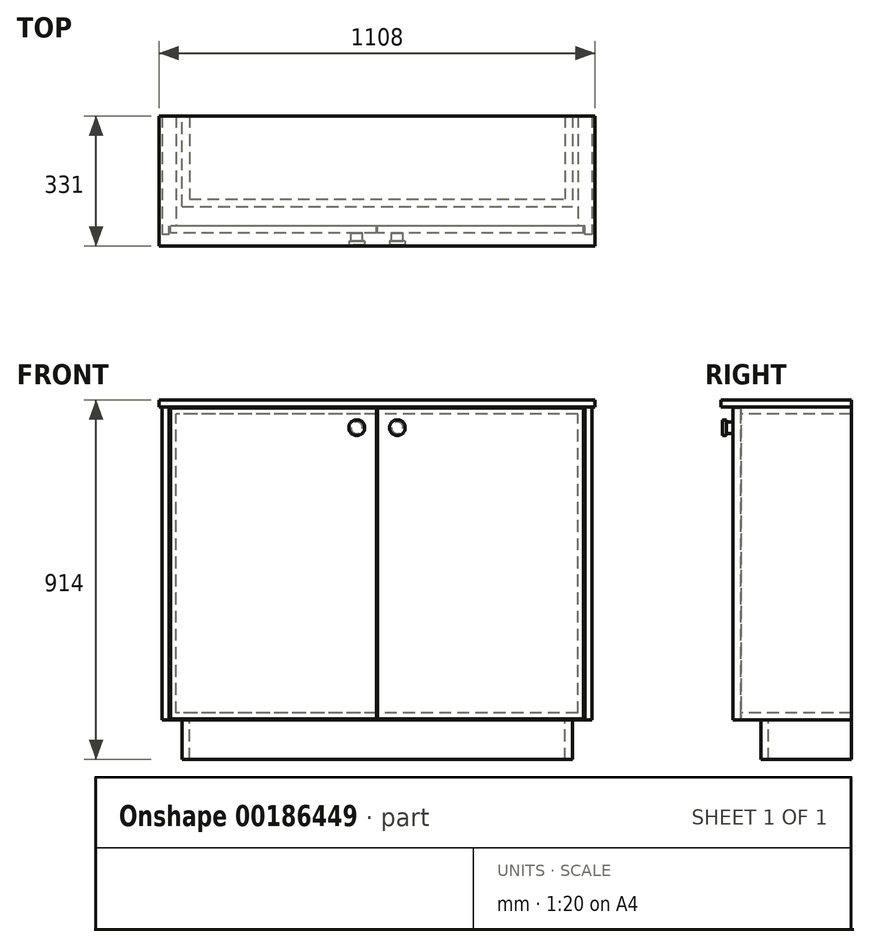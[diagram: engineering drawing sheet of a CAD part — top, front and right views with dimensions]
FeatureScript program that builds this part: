
annotation { "Feature Type Name" : "Feature", "Feature Type Description" : "" }
export const myFeature = defineFeature(function(context is Context, id is Id, definition is map)
    precondition{}
    {
        {
            var Q0;
            Q0=qCreatedBy(makeId("Front.planeOp"),FACE);
            var sketch = newSketch(context, id + "F0", { "sketchPlane" : qUnion([Q0])});
            skLineSegment(sketch, "E0.bottom", {"start": v(528, -398) * mm, "end": v(-528, -398) * mm});
            skLineSegment(sketch, "E0.top", {"start": v(528, 398) * mm, "end": v(-528, 398) * mm});
            skLineSegment(sketch, "E0.left", {"start": v(528, -398) * mm, "end": v(528, 398) * mm});
            skLineSegment(sketch, "E0.right", {"start": v(-528, -398) * mm, "end": v(-528, 398) * mm});
            skPoint(sketch, "E0.middle", {"position": v(0, 0) * mm});
            skLineSegment(sketch, "E1.0", {"start": v(510, -380) * mm, "end": v(-510, -380) * mm});
            skLineSegment(sketch, "E1.1", {"start": v(510, -380) * mm, "end": v(510, 380) * mm});
            skLineSegment(sketch, "E1.2", {"start": v(510, 380) * mm, "end": v(-510, 380) * mm});
            skLineSegment(sketch, "E1.3", {"start": v(-510, -380) * mm, "end": v(-510, 380) * mm});
            skLineSegment(sketch, "E2", {"start": v(510, 380) * mm, "end": v(510, 398) * mm});
            skLineSegment(sketch, "E3", {"start": v(510, -380) * mm, "end": v(510, -398) * mm});
            skLineSegment(sketch, "E4", {"start": v(-510, -380) * mm, "end": v(-510, -398) * mm});
            skLineSegment(sketch, "E5", {"start": v(-510, 380) * mm, "end": v(-510, 398) * mm});
            skSolve(sketch);
        }
        {
            var Q0;
            Q0=makeQuery(id+"F0.imprint","IMPRINT",FACE,{"disambiguationData":[TD([[makeQuery(id+"F0.imprint","IMPRINT",EDGE,{"derivedFrom":sQuery(id+"F0.wireOp",EDGE,"E1.2")}),-1.0]])]});
            extrude(context, id + "F1", {"entities" : qUnion([Q0]), "oppositeDirection" : true, "depth" : 280 * mm});
        }
        {
            var Q0;
            Q0 = qSketchRegion(id + "F0", true);
            extrude(context, id + "F2", {"entities" : qUnion([Q0]), "operationType" : NewBodyOperationType.ADD, "oppositeDirection" : true, "depth" : 280 * mm});
        }
        {
            var Q0;
            Q0=makeQuery(id+"F2.opExtrude","SWEPT_FACE",FACE,{"disambiguationData":[OSD([sQuery(id+"F0.wireOp",EDGE,"E0.left")])]});
            var sketch = newSketch(context, id + "F3", { "sketchPlane" : qUnion([Q0])});
            skLineSegment(sketch, "E6.bottom", {"start": v(0, 398) * mm, "end": v(280, 398) * mm});
            skLineSegment(sketch, "E6.top", {"start": v(0, -398) * mm, "end": v(280, -398) * mm});
            skLineSegment(sketch, "E6.left", {"start": v(0, 398) * mm, "end": v(0, -398) * mm});
            skLineSegment(sketch, "E6.right", {"start": v(280, 398) * mm, "end": v(280, -398) * mm});
            skSolve(sketch);
        }
        {
            var Q0;
            Q0=makeQuery(id+"F3.imprint","IMPRINT",FACE,{"disambiguationData":[TD([[makeQuery(id+"F3.imprint","IMPRINT",EDGE,{"derivedFrom":sQuery(id+"F3.wireOp",EDGE,"E6.bottom")}),1.0]])]});
            extrude(context, id + "F4", {"entities" : qUnion([Q0]), "operationType" : NewBodyOperationType.ADD, "depth" : 18 * mm});
        }
        {
            var Q0;
            Q0=makeQuery(id+"F2.opExtrude","SWEPT_FACE",FACE,{"disambiguationData":[OSD([sQuery(id+"F0.wireOp",EDGE,"E0.right")])]});
            var sketch = newSketch(context, id + "F5", { "sketchPlane" : qUnion([Q0])});
            skLineSegment(sketch, "E7.bottom", {"start": v(0, -398) * mm, "end": v(-280, -398) * mm});
            skLineSegment(sketch, "E7.top", {"start": v(0, 398) * mm, "end": v(-280, 398) * mm});
            skLineSegment(sketch, "E7.left", {"start": v(0, -398) * mm, "end": v(0, 398) * mm});
            skLineSegment(sketch, "E7.right", {"start": v(-280, -398) * mm, "end": v(-280, 398) * mm});
            skSolve(sketch);
        }
        {
            var Q0;
            Q0=makeQuery(id+"F5.imprint","IMPRINT",FACE,{"disambiguationData":[TD([[makeQuery(id+"F5.imprint","IMPRINT",EDGE,{"derivedFrom":sQuery(id+"F5.wireOp",EDGE,"E7.bottom")}),1.0]])]});
            extrude(context, id + "F6", {"entities" : qUnion([Q0]), "operationType" : NewBodyOperationType.ADD, "depth" : 18 * mm});
        }
        {
            var Q0;
            {var subQ0=sQuery(id+"F0.wireOp",EDGE,"E0.top");Q0=makeQuery(id+"F6.boolean.opBoolean","MERGE",FACE,{"derivedFrom":[makeQuery(id+"F4.boolean.opBoolean","MERGE",FACE,{"derivedFrom":[makeQuery(id+"F2.boolean.opBoolean","MERGE",FACE,{"derivedFrom":[makeQuery(id+"F1.opExtrude","SWEPT_FACE",FACE,{"disambiguationData":[OSD([subQ0])]}),makeQuery(id+"F2.opExtrude","SWEPT_FACE",FACE,{"disambiguationData":[OSD([subQ0])]})]}),makeQuery(id+"F4.opExtrude","SWEPT_FACE",FACE,{"disambiguationData":[OSD([sQuery(id+"F3.wireOp",EDGE,"E6.bottom")])]})]}),makeQuery(id+"F6.opExtrude","SWEPT_FACE",FACE,{"disambiguationData":[OSD([sQuery(id+"F5.wireOp",EDGE,"E7.top")])]})]});}
            var sketch = newSketch(context, id + "F7", { "sketchPlane" : qUnion([Q0])});
            skLineSegment(sketch, "E8.bottom", {"start": v(-546, 280) * mm, "end": v(554, 280) * mm});
            skLineSegment(sketch, "E8.top", {"start": v(-546, -30) * mm, "end": v(554, -30) * mm});
            skLineSegment(sketch, "E8.left", {"start": v(-546, 280) * mm, "end": v(-546, -30) * mm});
            skLineSegment(sketch, "E8.right", {"start": v(554, 280) * mm, "end": v(554, -30) * mm});
            skSolve(sketch);
        }
        {
            var Q0;
            {var subQ1=sQuery(id+"F3.wireOp",EDGE,"E6.bottom");var subQ2=makeQuery(id+"F4.opExtrude","CAP_EDGE",EDGE,{"disambiguationData":[OSD([subQ1])],"isStart":false});Q0=makeQuery(id+"F7.imprint","IMPRINT",FACE,{"disambiguationData":[TD([[makeQuery(id+"F7.imprint","IMPRINT",EDGE,{"derivedFrom":subQ2}),-1.0]])]});}
            var Q1;
            Q1=makeQuery(id+"F7.imprint","IMPRINT",FACE,{"disambiguationData":[TD([[makeQuery(id+"F7.imprint","IMPRINT",EDGE,{"derivedFrom":sQuery(id+"F7.wireOp",EDGE,"E8.top")}),1.0]])]});
            extrude(context, id + "F8", {"entities" : qUnion([Q0, Q1]), "operationType" : NewBodyOperationType.ADD, "depth" : 18 * mm});
        }
        {
            var Q0;
            {var subQ0=sQuery(id+"F0.wireOp",EDGE,"E1.2");var subQ1=sQuery(id+"F0.wireOp",EDGE,"E0.top");Q0=makeQuery(id+"F6.boolean.opBoolean","MERGE",FACE,{"derivedFrom":[makeQuery(id+"F4.boolean.opBoolean","MERGE",FACE,{"derivedFrom":[makeQuery(id+"F2.boolean.opBoolean","MERGE",FACE,{"derivedFrom":[makeQuery(id+"F1.opExtrude","CAP_FACE",FACE,{"disambiguationData":[OSD([subQ1,subQ0,sQuery(id+"F0.wireOp",EDGE,"E2"),sQuery(id+"F0.wireOp",EDGE,"E5")])],"isStart":true}),makeQuery(id+"F2.opExtrude","CAP_FACE",FACE,{"disambiguationData":[OSD([sQuery(id+"F0.wireOp",EDGE,"E0.bottom"),subQ1,sQuery(id+"F0.wireOp",EDGE,"E0.left"),sQuery(id+"F0.wireOp",EDGE,"E0.right"),sQuery(id+"F0.wireOp",EDGE,"E1.0"),sQuery(id+"F0.wireOp",EDGE,"E1.1"),subQ0,sQuery(id+"F0.wireOp",EDGE,"E1.3")])],"isStart":true})]}),makeQuery(id+"F4.opExtrude","SWEPT_FACE",FACE,{"disambiguationData":[OSD([sQuery(id+"F3.wireOp",EDGE,"E6.left")])]})]}),makeQuery(id+"F6.opExtrude","SWEPT_FACE",FACE,{"disambiguationData":[OSD([sQuery(id+"F5.wireOp",EDGE,"E7.left")])]})]});}
            var sketch = newSketch(context, id + "F9", { "sketchPlane" : qUnion([Q0])});
            skLineSegment(sketch, "E9.bottom", {"start": v(-546, 398) * mm, "end": v(-528, 398) * mm});
            skLineSegment(sketch, "E9.top", {"start": v(-546, -398) * mm, "end": v(-528, -398) * mm});
            skLineSegment(sketch, "E9.left", {"start": v(-546, 398) * mm, "end": v(-546, -398) * mm});
            skLineSegment(sketch, "E9.right", {"start": v(-528, 398) * mm, "end": v(-528, -398) * mm});
            skLineSegment(sketch, "E10.bottom", {"start": v(546, 398) * mm, "end": v(528, 398) * mm});
            skLineSegment(sketch, "E10.top", {"start": v(546, -398) * mm, "end": v(528, -398) * mm});
            skLineSegment(sketch, "E10.left", {"start": v(546, 398) * mm, "end": v(546, -398) * mm});
            skLineSegment(sketch, "E10.right", {"start": v(528, 398) * mm, "end": v(528, -398) * mm});
            skSolve(sketch);
        }
        {
            var Q0;
            Q0=makeQuery(id+"F9.imprint","IMPRINT",FACE,{"disambiguationData":[TD([[makeQuery(id+"F9.imprint","IMPRINT",EDGE,{"derivedFrom":sQuery(id+"F9.wireOp",EDGE,"E9.bottom")}),1.0]])]});
            extrude(context, id + "F10", {"entities" : qUnion([Q0]), "operationType" : NewBodyOperationType.ADD, "depth" : 21 * mm});
        }
        {
            var Q0;
            Q0=makeQuery(id+"F9.imprint","IMPRINT",FACE,{"disambiguationData":[TD([[makeQuery(id+"F9.imprint","IMPRINT",EDGE,{"derivedFrom":sQuery(id+"F9.wireOp",EDGE,"E10.bottom")}),1.0]])]});
            extrude(context, id + "F11", {"entities" : qUnion([Q0]), "operationType" : NewBodyOperationType.ADD, "depth" : 21 * mm});
        }
        {
            var Q0;
            Q0=makeQuery(id+"F8.opExtrude","SWEPT_FACE",FACE,{"disambiguationData":[OSD([sQuery(id+"F7.wireOp",EDGE,"E8.top")])]});
            extrude(context, id + "F12", {"entities" : qUnion([Q0]), "operationType" : NewBodyOperationType.ADD, "depth" : 21 * mm});
        }
        {
            var Q0;
            Q0=makeQuery(id+"F11.boolean.opBoolean","MERGE",FACE,{"derivedFrom":[makeQuery(id+"F10.boolean.opBoolean","MERGE",FACE,{"derivedFrom":[makeQuery(id+"F6.boolean.opBoolean","MERGE",FACE,{"derivedFrom":[makeQuery(id+"F4.boolean.opBoolean","MERGE",FACE,{"derivedFrom":[makeQuery(id+"F2.opExtrude","SWEPT_FACE",FACE,{"disambiguationData":[OSD([sQuery(id+"F0.wireOp",EDGE,"E0.bottom")])]}),makeQuery(id+"F4.opExtrude","SWEPT_FACE",FACE,{"disambiguationData":[OSD([sQuery(id+"F3.wireOp",EDGE,"E6.top")])]})]}),makeQuery(id+"F6.opExtrude","SWEPT_FACE",FACE,{"disambiguationData":[OSD([sQuery(id+"F5.wireOp",EDGE,"E7.bottom")])]})]}),makeQuery(id+"F10.opExtrude","SWEPT_FACE",FACE,{"disambiguationData":[OSD([sQuery(id+"F9.wireOp",EDGE,"E9.top")])]})]}),makeQuery(id+"F11.opExtrude","SWEPT_FACE",FACE,{"disambiguationData":[OSD([sQuery(id+"F9.wireOp",EDGE,"E10.top")])]})]});
            var sketch = newSketch(context, id + "F13", { "sketchPlane" : qUnion([Q0])});
            skLineSegment(sketch, "E11.bottom", {"start": v(-496, -280) * mm, "end": v(496, -280) * mm});
            skLineSegment(sketch, "E11.top", {"start": v(-496, -50) * mm, "end": v(496, -50) * mm});
            skLineSegment(sketch, "E11.right", {"start": v(496, -280) * mm, "end": v(496, -50) * mm});
            skLineSegment(sketch, "E12.0", {"start": v(477, -306.99) * mm, "end": v(477, -69) * mm});
            skLineSegment(sketch, "E12.1", {"start": v(-477, -69) * mm, "end": v(477, -69) * mm});
            skLineSegment(sketch, "E13.0", {"start": v(-477, -280) * mm, "end": v(-477, -69) * mm});
            skLineSegment(sketch, "E14", {"start": v(-496, -50) * mm, "end": v(-496, -280) * mm});
            skSolve(sketch);
        }
        {
            var Q0;
            Q0=makeQuery(id+"F13.imprint","IMPRINT",FACE,{"disambiguationData":[TD([[makeQuery(id+"F13.imprint","IMPRINT",EDGE,{"derivedFrom":sQuery(id+"F13.wireOp",EDGE,"E11.top")}),-1.0]])]});
            var Q1;
            Q1=sQuery(id+"F13.wireOp",EDGE,"E12.0");
            var Q2;
            Q2=sQuery(id+"F13.wireOp",EDGE,"E11.right");
            var Q3;
            Q3=sQuery(id+"F13.wireOp",EDGE,"E11.top");
            var Q4;
            Q4=sQuery(id+"F13.wireOp",EDGE,"E12.1");
            var Q5;
            Q5=sQuery(id+"F13.wireOp",EDGE,"E14");
            var Q6;
            Q6=sQuery(id+"F13.wireOp",EDGE,"E13.0");
            extrude(context, id + "F14", {"entities" : qUnion([Q0]), "operationType" : NewBodyOperationType.ADD, "surfaceEntities" : qUnion([Q1, Q2, Q3, Q4, Q5, Q6]), "depth" : 100 * mm});
        }
        {
            var Q0;
            {var subQ0=sQuery(id+"F0.wireOp",EDGE,"E1.2");var subQ1=sQuery(id+"F0.wireOp",EDGE,"E0.top");Q0=makeQuery(id+"F6.boolean.opBoolean","MERGE",FACE,{"derivedFrom":[makeQuery(id+"F4.boolean.opBoolean","MERGE",FACE,{"derivedFrom":[makeQuery(id+"F2.boolean.opBoolean","MERGE",FACE,{"derivedFrom":[makeQuery(id+"F1.opExtrude","CAP_FACE",FACE,{"disambiguationData":[OSD([subQ1,subQ0,sQuery(id+"F0.wireOp",EDGE,"E2"),sQuery(id+"F0.wireOp",EDGE,"E5")])],"isStart":true}),makeQuery(id+"F2.opExtrude","CAP_FACE",FACE,{"disambiguationData":[OSD([sQuery(id+"F0.wireOp",EDGE,"E0.bottom"),subQ1,sQuery(id+"F0.wireOp",EDGE,"E0.left"),sQuery(id+"F0.wireOp",EDGE,"E0.right"),sQuery(id+"F0.wireOp",EDGE,"E1.0"),sQuery(id+"F0.wireOp",EDGE,"E1.1"),subQ0,sQuery(id+"F0.wireOp",EDGE,"E1.3")])],"isStart":true})]}),makeQuery(id+"F4.opExtrude","SWEPT_FACE",FACE,{"disambiguationData":[OSD([sQuery(id+"F3.wireOp",EDGE,"E6.left")])]})]}),makeQuery(id+"F6.opExtrude","SWEPT_FACE",FACE,{"disambiguationData":[OSD([sQuery(id+"F5.wireOp",EDGE,"E7.left")])]})]});}
            var sketch = newSketch(context, id + "F15", { "sketchPlane" : qUnion([Q0])});
            skLineSegment(sketch, "E15.bottom", {"start": v(525, 395) * mm, "end": v(-525, 395) * mm});
            skLineSegment(sketch, "E15.top", {"start": v(525, -395) * mm, "end": v(-525, -395) * mm});
            skLineSegment(sketch, "E15.left", {"start": v(525, 395) * mm, "end": v(525, -395) * mm});
            skLineSegment(sketch, "E15.right", {"start": v(-525, 395) * mm, "end": v(-525, -395) * mm});
            skPoint(sketch, "E15.middle", {"position": v(0, 0) * mm});
            skLineSegment(sketch, "E16", {"start": v(0, -395) * mm, "end": v(0, 395) * mm});
            skLineSegment(sketch, "E17.0", {"start": v(1.5, -395) * mm, "end": v(1.5, 395) * mm});
            skLineSegment(sketch, "E18.0", {"start": v(-1.5, -395) * mm, "end": v(-1.5, 395) * mm});
            skSolve(sketch);
        }
        {
            var Q0;
            {var subQ5=sQuery(id+"F15.wireOp",EDGE,"E15.right");Q0=makeQuery(id+"F15.imprint","IMPRINT",FACE,{"disambiguationData":[TD([[makeQuery(id+"F15.imprint","IMPRINT",EDGE,{"derivedFrom":subQ5}),1.0]])]});}
            var Q1;
            {var subQ5=makeQuery(id+"F2.opExtrude","CAP_EDGE",EDGE,{"disambiguationData":[OSD([sQuery(id+"F0.wireOp",EDGE,"E1.3")])],"isStart":true});Q1=makeQuery(id+"F15.imprint","IMPRINT",FACE,{"disambiguationData":[TD([[makeQuery(id+"F15.imprint","IMPRINT",EDGE,{"derivedFrom":subQ5}),-1.0]])]});}
            extrude(context, id + "F16", {"entities" : qUnion([Q0, Q1]), "operationType" : NewBodyOperationType.ADD, "depth" : 18 * mm});
        }
        {
            var Q0;
            {var subQ5=sQuery(id+"F15.wireOp",EDGE,"E15.left");Q0=makeQuery(id+"F15.imprint","IMPRINT",FACE,{"disambiguationData":[TD([[makeQuery(id+"F15.imprint","IMPRINT",EDGE,{"derivedFrom":subQ5}),-1.0]])]});}
            var Q1;
            {var subQ5=makeQuery(id+"F2.opExtrude","CAP_EDGE",EDGE,{"disambiguationData":[OSD([sQuery(id+"F0.wireOp",EDGE,"E1.1")])],"isStart":true});Q1=makeQuery(id+"F15.imprint","IMPRINT",FACE,{"disambiguationData":[TD([[makeQuery(id+"F15.imprint","IMPRINT",EDGE,{"derivedFrom":subQ5}),1.0]])]});}
            extrude(context, id + "F17", {"entities" : qUnion([Q0, Q1]), "operationType" : NewBodyOperationType.ADD, "depth" : 18 * mm});
        }
        {
            var Q0;
            Q0=makeQuery(id+"F16.opExtrude","CAP_FACE",FACE,{"disambiguationData":[OSD([sQuery(id+"F15.wireOp",EDGE,"E15.bottom"),sQuery(id+"F15.wireOp",EDGE,"E15.top"),sQuery(id+"F15.wireOp",EDGE,"E15.right"),sQuery(id+"F15.wireOp",EDGE,"E18.0")])],"isStart":false});
            var sketch = newSketch(context, id + "F18", { "sketchPlane" : qUnion([Q0])});
            skLineSegment(sketch, "E19.bottom", {"start": v(-1.5, 395) * mm, "end": v(-51.5, 395) * mm, "construction": true});
            skLineSegment(sketch, "E19.top", {"start": v(-1.5, 345) * mm, "end": v(-51.5, 345) * mm, "construction": true});
            skLineSegment(sketch, "E19.left", {"start": v(-1.5, 395) * mm, "end": v(-1.5, 345) * mm, "construction": true});
            skLineSegment(sketch, "E19.right", {"start": v(-51.5, 395) * mm, "end": v(-51.5, 345) * mm, "construction": true});
            skCircle(sketch, "E20", {"center": v(-51.5, 345) * mm, "radius": 15 * mm});
            skSolve(sketch);
        }
        {
            var Q0;
            Q0=makeQuery(id+"F18.imprint","IMPRINT",FACE,{"disambiguationData":[TD([[makeQuery(id+"F18.imprint","IMPRINT",EDGE,{"derivedFrom":sQuery(id+"F18.wireOp",EDGE,"E20")}),1.0]])]});
            extrude(context, id + "F19", {"entities" : qUnion([Q0]), "operationType" : NewBodyOperationType.ADD, "depth" : 30 * mm});
        }
        {
            var Q0;
            Q0=makeQuery(id+"F19.opExtrude","CAP_FACE",FACE,{"disambiguationData":[OSD([sQuery(id+"F18.wireOp",EDGE,"E20")])],"isStart":false});
            var sketch = newSketch(context, id + "F20", { "sketchPlane" : qUnion([Q0])});
            skCircle(sketch, "E21", {"center": v(-51.5, 345) * mm, "radius": 20 * mm});
            skSolve(sketch);
        }
        {
            var Q0;
            Q0=makeQuery(id+"F20.imprint","IMPRINT",FACE,{"disambiguationData":[TD([[makeQuery(id+"F20.imprint","IMPRINT",EDGE,{"derivedFrom":sQuery(id+"F20.wireOp",EDGE,"E21")}),1.0]])]});
            extrude(context, id + "F21", {"entities" : qUnion([Q0]), "operationType" : NewBodyOperationType.ADD, "oppositeDirection" : true, "depth" : 10 * mm});
        }
        {
            var Q0;
            Q0=makeQuery(id+"F1.opExtrude","SWEPT_BODY",BODY,{"disambiguationData":[OSD([sQuery(id+"F0.wireOp",EDGE,"E0.top"),sQuery(id+"F0.wireOp",EDGE,"E1.2"),sQuery(id+"F0.wireOp",EDGE,"E2"),sQuery(id+"F0.wireOp",EDGE,"E5")])]});
            var Q1;
            Q1=qCreatedBy(makeId("Right.planeOp"),FACE);
            mirror(context, id + "F22", {"operationType" : NewBodyOperationType.ADD, "entities" : qUnion([Q0]), "mirrorPlane" : qUnion([Q1])});
        }
    });
